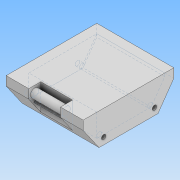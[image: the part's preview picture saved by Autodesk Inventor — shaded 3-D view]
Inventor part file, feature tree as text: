
AUTODESK INVENTOR PART (.ipt)
format: ipt  version: 2021 (Build 250183000, 183)  size: 160,256 bytes
history: native  units: mm
features: extrude x6, other x4, sketch x4, plane x1
ambient origin geometry x8: Origin, YZ Plane, XZ Plane, XY Plane, X Axis, Y Axis, Z Axis, Center Point
bodies: Body1 (feature_tree)
feature tree (15):
  other  "實體1"
  sketch  "草圖1"
  extrude  "擠出1"  Depth=1300.0mm
  extrude  "擠出2"  Depth=2000.0mm
  extrude  "擠出3"  Depth=500.0mm
  extrude  "擠出4"  Depth=200.0mm
  plane  "工作平面1"
  extrude  "擠出5"  Depth=1700.0mm TaperAngle=0.0deg
  extrude  "擠出6"  Depth=180.0mm
  other  "螺紋2"
  sketch  "草圖2"
  sketch  "草圖4"
  sketch  "草圖5"
  other  "投影切割邊1"
  other  "投影切割邊3"
